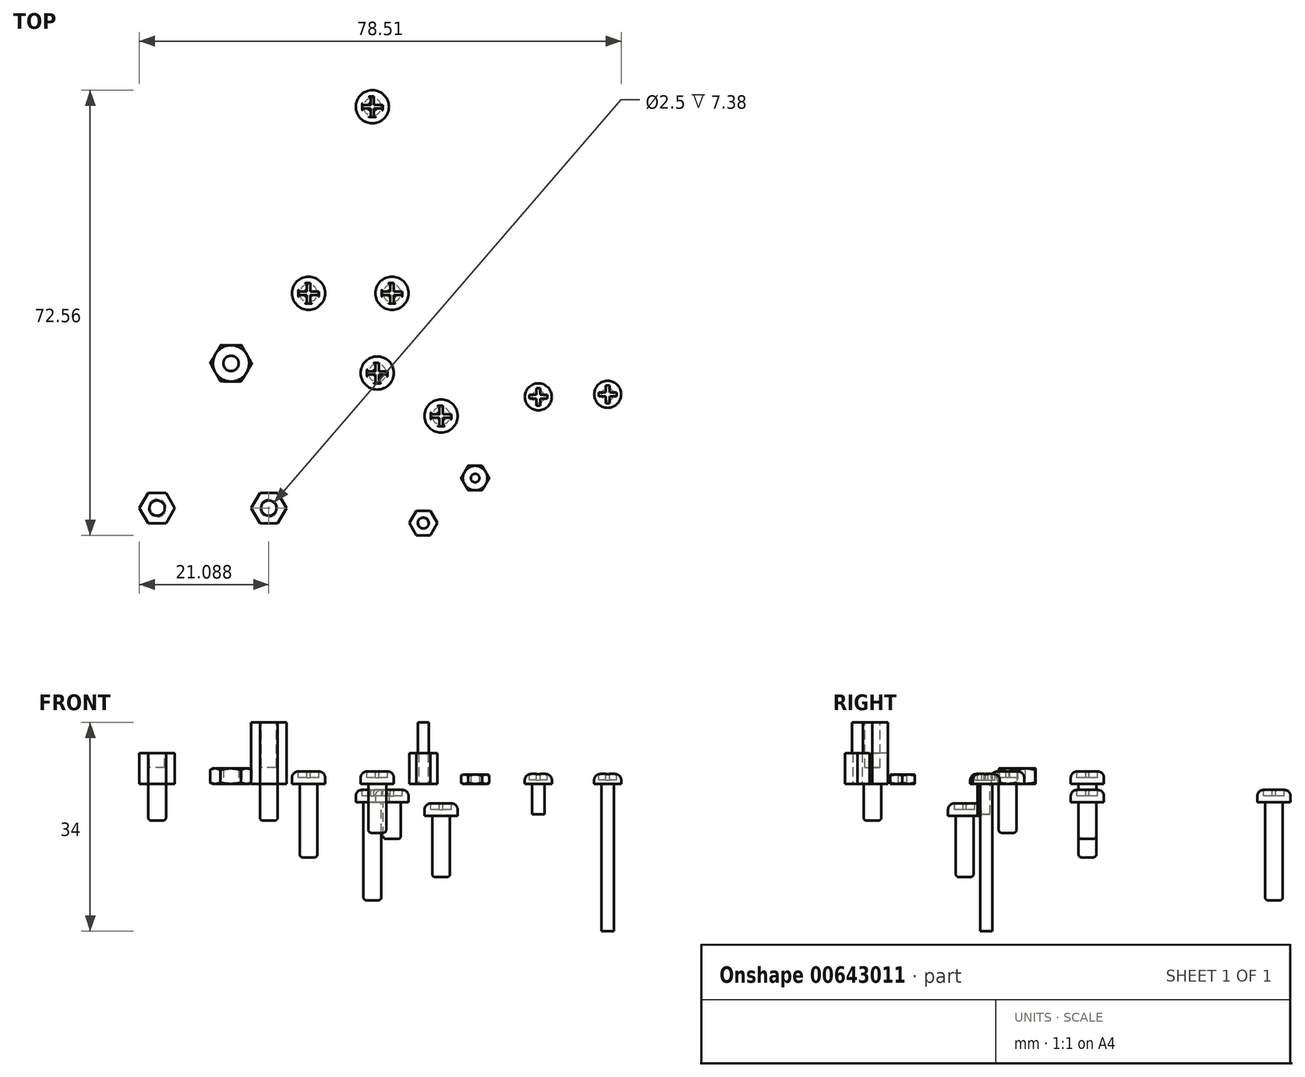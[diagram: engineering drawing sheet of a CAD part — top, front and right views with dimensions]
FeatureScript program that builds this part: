
annotation { "Feature Type Name" : "Feature", "Feature Type Description" : "" }
export const myFeature = defineFeature(function(context is Context, id is Id, definition is map)
    precondition{}
    {
        {
            var Q0;
            Q0=qCreatedBy(makeId("Top.planeOp"),FACE);
            var sketch = newSketch(context, id + "F0", { "sketchPlane" : qUnion([Q0])});
            skCircle(sketch, "E0.cCircle", {"center": v(-52.55, 30.34) * mm, "radius": 2.95 * mm, "construction": true});
            skLineSegment(sketch, "E0.0", {"start": v(-49.14, 30.28) * mm, "end": v(-50.9, 27.36) * mm});
            skLineSegment(sketch, "E0.1", {"start": v(-50.9, 27.36) * mm, "end": v(-54.3, 27.43) * mm});
            skLineSegment(sketch, "E0.2", {"start": v(-54.3, 27.43) * mm, "end": v(-55.95, 30.4) * mm});
            skLineSegment(sketch, "E0.3", {"start": v(-55.95, 30.4) * mm, "end": v(-54.2, 33.32) * mm});
            skLineSegment(sketch, "E0.4", {"start": v(-54.2, 33.32) * mm, "end": v(-50.79, 33.26) * mm});
            skLineSegment(sketch, "E0.5", {"start": v(-50.79, 33.26) * mm, "end": v(-49.14, 30.28) * mm});
            skPoint(sketch, "E0.0.midPoint", {"position": v(-50.02, 28.82) * mm});
            skCircle(sketch, "E1", {"center": v(-52.55, 30.34) * mm, "radius": 1.25 * mm});
            skSolve(sketch);
        }
        {
            var Q0;
            Q0=makeQuery(id+"F0.imprint","IMPRINT",FACE,{"disambiguationData":[TD([[makeQuery(id+"F0.imprint","IMPRINT",EDGE,{"derivedFrom":sQuery(id+"F0.wireOp",EDGE,"E0.0")}),-1.0]])]});
            extrude(context, id + "F1", {"entities" : qUnion([Q0]), "depth" : 2.5 * mm, "offsetDistance" : 25 * mm});
        }
        {
            var Q0;
            Q0=qCreatedBy(makeId("Top.planeOp"),FACE);
            var sketch = newSketch(context, id + "F2", { "sketchPlane" : qUnion([Q0])});
            skCircle(sketch, "E2", {"center": v(-39.92, 41.77) * mm, "radius": 2.7 * mm});
            skSolve(sketch);
        }
        {
            var Q0;
            Q0=makeQuery(id+"F2.imprint","IMPRINT",FACE,{"disambiguationData":[TD([[makeQuery(id+"F2.imprint","IMPRINT",EDGE,{"derivedFrom":sQuery(id+"F2.wireOp",EDGE,"E2")}),1.0]])]});
            extrude(context, id + "F3", {"entities" : qUnion([Q0]), "depth" : 2 * mm, "offsetDistance" : 25 * mm});
        }
        {
            var Q0;
            Q0=makeQuery(id+"F3.opExtrude","CAP_EDGE",EDGE,{"disambiguationData":[OSD([sQuery(id+"F2.wireOp",EDGE,"E2")])],"isStart":false});
            fillet(context, id + "F4", {"entities" : qUnion([Q0]), "radius" : 1 * mm, "tangentPropagation" : true, "allowEdgeOverflow" : false});
        }
        {
            var Q0;
            Q0=makeQuery(id+"F3.opExtrude","CAP_FACE",FACE,{"disambiguationData":[OSD([sQuery(id+"F2.wireOp",EDGE,"E2")])],"isStart":false});
            var sketch = newSketch(context, id + "F5", { "sketchPlane" : qUnion([Q0])});
            skLineSegment(sketch, "E3.bottom", {"start": v(-40.19, 43.45) * mm, "end": v(-39.65, 43.45) * mm});
            skLineSegment(sketch, "E3.top", {"start": v(-40.19, 40.1) * mm, "end": v(-39.65, 40.1) * mm});
            skLineSegment(sketch, "E3.left", {"start": v(-40.19, 43.45) * mm, "end": v(-40.19, 42.04) * mm});
            skLineSegment(sketch, "E3.right", {"start": v(-39.65, 43.45) * mm, "end": v(-39.65, 42.04) * mm});
            skPoint(sketch, "E3.middle", {"position": v(-39.92, 41.77) * mm});
            skLineSegment(sketch, "E4.bottom", {"start": v(-38.24, 42.04) * mm, "end": v(-38.24, 41.5) * mm});
            skLineSegment(sketch, "E4.top", {"start": v(-41.6, 42.04) * mm, "end": v(-41.6, 41.5) * mm});
            skLineSegment(sketch, "E4.left", {"start": v(-38.24, 42.04) * mm, "end": v(-39.65, 42.04) * mm});
            skLineSegment(sketch, "E4.right", {"start": v(-38.24, 41.5) * mm, "end": v(-39.65, 41.5) * mm});
            skLineSegment(sketch, "E5.trimOffspring", {"start": v(-40.19, 42.04) * mm, "end": v(-41.6, 42.04) * mm});
            skLineSegment(sketch, "E6.trimOffspring", {"start": v(-40.19, 41.5) * mm, "end": v(-40.19, 40.1) * mm});
            skLineSegment(sketch, "E7.trimOffspring", {"start": v(-40.19, 41.5) * mm, "end": v(-41.6, 41.5) * mm});
            skLineSegment(sketch, "E8.trimOffspring", {"start": v(-39.65, 41.5) * mm, "end": v(-39.65, 40.1) * mm});
            skSolve(sketch);
        }
        {
            var Q0;
            Q0=makeQuery(id+"F5.imprint","IMPRINT",FACE,{"disambiguationData":[TD([[makeQuery(id+"F5.imprint","IMPRINT",EDGE,{"derivedFrom":sQuery(id+"F5.wireOp",EDGE,"E3.bottom")}),-1.0]])]});
            extrude(context, id + "F6", {"entities" : qUnion([Q0]), "operationType" : NewBodyOperationType.REMOVE, "oppositeDirection" : true, "depth" : 1 * mm, "offsetDistance" : 25 * mm});
        }
        {
            var Q0;
            Q0=makeQuery(id+"F6.boolean.opBoolean","COPY",EDGE,{"derivedFrom":makeQuery(id+"F6.opExtrude","CAP_EDGE",EDGE,{"disambiguationData":[OSD([sQuery(id+"F5.wireOp",EDGE,"E4.left")])],"isStart":true})});
            var Q1;
            Q1=makeQuery(id+"F6.boolean.opBoolean","COPY",EDGE,{"derivedFrom":makeQuery(id+"F6.opExtrude","CAP_EDGE",EDGE,{"disambiguationData":[OSD([sQuery(id+"F5.wireOp",EDGE,"E3.right")])],"isStart":true})});
            var Q2;
            Q2=makeQuery(id+"F6.boolean.opBoolean","COPY",EDGE,{"derivedFrom":makeQuery(id+"F6.opExtrude","CAP_EDGE",EDGE,{"disambiguationData":[OSD([sQuery(id+"F5.wireOp",EDGE,"E3.left")])],"isStart":true})});
            var Q3;
            Q3=makeQuery(id+"F6.boolean.opBoolean","COPY",EDGE,{"derivedFrom":makeQuery(id+"F6.opExtrude","CAP_EDGE",EDGE,{"disambiguationData":[OSD([sQuery(id+"F5.wireOp",EDGE,"E5.trimOffspring")])],"isStart":true})});
            var Q4;
            Q4=makeQuery(id+"F6.boolean.opBoolean","COPY",EDGE,{"derivedFrom":makeQuery(id+"F6.opExtrude","CAP_EDGE",EDGE,{"disambiguationData":[OSD([sQuery(id+"F5.wireOp",EDGE,"E7.trimOffspring")])],"isStart":true})});
            var Q5;
            Q5=makeQuery(id+"F6.boolean.opBoolean","COPY",EDGE,{"derivedFrom":makeQuery(id+"F6.opExtrude","CAP_EDGE",EDGE,{"disambiguationData":[OSD([sQuery(id+"F5.wireOp",EDGE,"E6.trimOffspring")])],"isStart":true})});
            var Q6;
            Q6=makeQuery(id+"F6.boolean.opBoolean","COPY",EDGE,{"derivedFrom":makeQuery(id+"F6.opExtrude","CAP_EDGE",EDGE,{"disambiguationData":[OSD([sQuery(id+"F5.wireOp",EDGE,"E8.trimOffspring")])],"isStart":true})});
            var Q7;
            Q7=makeQuery(id+"F6.boolean.opBoolean","COPY",EDGE,{"derivedFrom":makeQuery(id+"F6.opExtrude","CAP_EDGE",EDGE,{"disambiguationData":[OSD([sQuery(id+"F5.wireOp",EDGE,"E4.right")])],"isStart":true})});
            fillet(context, id + "F7", {"entities" : qUnion([Q0, Q1, Q2, Q3, Q4, Q5, Q6, Q7]), "radius" : 0.3 * mm, "tangentPropagation" : true, "allowEdgeOverflow" : false});
        }
        {
            var Q0;
            Q0=makeQuery(id+"F3.opExtrude","CAP_FACE",FACE,{"disambiguationData":[OSD([sQuery(id+"F2.wireOp",EDGE,"E2")])],"isStart":true});
            var sketch = newSketch(context, id + "F8", { "sketchPlane" : qUnion([Q0])});
            skCircle(sketch, "E9.0", {"center": v(-39.92, -41.77) * mm, "radius": 2.7 * mm});
            skCircle(sketch, "E10", {"center": v(-39.92, -41.77) * mm, "radius": 1.45 * mm});
            skSolve(sketch);
        }
        {
            var Q0;
            Q0=makeQuery(id+"F3.opExtrude","SWEPT_BODY",BODY,{"disambiguationData":[OSD([sQuery(id+"F2.wireOp",EDGE,"E2")])]});
            transform(context, id + "F9", {"entities" : qUnion([Q0]), "transformType" : TransformType.TRANSLATION_3D, "dx" : 13.6 * mm, "dy" : 0 * mm, "dz" : -3 * mm, "makeCopy" : true});
        }
        {
            var Q0;
            Q0=makeQuery(id+"F9.opPattern","COPY",BODY,{"derivedFrom":makeQuery(id+"F3.opExtrude","SWEPT_BODY",BODY,{"disambiguationData":[OSD([sQuery(id+"F2.wireOp",EDGE,"E2")])]}),"instanceName":"1"});
            transform(context, id + "F10", {"entities" : qUnion([Q0]), "transformType" : TransformType.TRANSLATION_3D, "dx" : -3.2 * mm, "dy" : 30.4 * mm, "dz" : 0 * mm, "makeCopy" : true});
        }
        {
            var Q0;
            Q0=makeQuery(id+"F3.opExtrude","SWEPT_BODY",BODY,{"disambiguationData":[OSD([sQuery(id+"F2.wireOp",EDGE,"E2")])]});
            transform(context, id + "F11", {"entities" : qUnion([Q0]), "transformType" : TransformType.TRANSLATION_3D, "dx" : 16.3 * mm, "dy" : -46.7 * mm, "dz" : 0 * mm, "makeCopy" : true});
        }
        {
            var Q0;
            Q0=makeQuery(id+"F3.opExtrude","SWEPT_BODY",BODY,{"disambiguationData":[OSD([sQuery(id+"F2.wireOp",EDGE,"E2")])]});
            transform(context, id + "F12", {"entities" : qUnion([Q0]), "transformType" : TransformType.TRANSLATION_3D, "dx" : 11.2 * mm, "dy" : -13 * mm, "dz" : 0 * mm, "makeCopy" : true});
        }
        {
            var Q0;
            Q0=makeQuery(id+"F8.imprint","IMPRINT",FACE,{"disambiguationData":[TD([[makeQuery(id+"F8.imprint","IMPRINT",EDGE,{"derivedFrom":sQuery(id+"F8.wireOp",EDGE,"E10")}),1.0]])]});
            extrude(context, id + "F13", {"entities" : qUnion([Q0]), "operationType" : NewBodyOperationType.ADD, "depth" : 12 * mm, "offsetDistance" : 25 * mm});
        }
        {
            var Q0;
            Q0=makeQuery(id+"F13.opExtrude","CAP_EDGE",EDGE,{"disambiguationData":[OSD([sQuery(id+"F8.wireOp",EDGE,"E10")])],"isStart":false});
            fillet(context, id + "F14", {"entities" : qUnion([Q0]), "radius" : 0.5 * mm, "tangentPropagation" : true, "allowEdgeOverflow" : false});
        }
        {
            var Q0;
            Q0=makeQuery(id+"F9.opPattern","COPY",FACE,{"derivedFrom":makeQuery(id+"F3.opExtrude","CAP_FACE",FACE,{"disambiguationData":[OSD([sQuery(id+"F2.wireOp",EDGE,"E2")])],"isStart":true}),"instanceName":"1"});
            var sketch = newSketch(context, id + "F15", { "sketchPlane" : qUnion([Q0])});
            skCircle(sketch, "E11.0", {"center": v(-26.32, -41.77) * mm, "radius": 2.7 * mm});
            skCircle(sketch, "E12", {"center": v(-26.32, -41.77) * mm, "radius": 1.45 * mm});
            skSolve(sketch);
        }
        {
            var Q0;
            Q0=makeQuery(id+"F15.imprint","IMPRINT",FACE,{"disambiguationData":[TD([[makeQuery(id+"F15.imprint","IMPRINT",EDGE,{"derivedFrom":sQuery(id+"F15.wireOp",EDGE,"E12")}),1.0]])]});
            extrude(context, id + "F16", {"entities" : qUnion([Q0]), "operationType" : NewBodyOperationType.ADD, "depth" : 6 * mm, "offsetDistance" : 25 * mm});
        }
        {
            var Q0;
            Q0=makeQuery(id+"F16.opExtrude","CAP_EDGE",EDGE,{"disambiguationData":[OSD([sQuery(id+"F15.wireOp",EDGE,"E12")])],"isStart":false});
            fillet(context, id + "F17", {"entities" : qUnion([Q0]), "radius" : 0.5 * mm, "tangentPropagation" : true, "allowEdgeOverflow" : false});
        }
        {
            var Q0;
            Q0=makeQuery(id+"F11.opPattern","COPY",BODY,{"derivedFrom":makeQuery(id+"F3.opExtrude","SWEPT_BODY",BODY,{"disambiguationData":[OSD([sQuery(id+"F2.wireOp",EDGE,"E2")])]}),"instanceName":"1"});
            transform(context, id + "F18", {"entities" : qUnion([Q0]), "transformType" : TransformType.TRANSLATION_3D, "dx" : 7.2 * mm, "dy" : 0 * mm, "dz" : 30.6 * mm, "makeCopy" : false});
        }
        {
            var Q0;
            Q0=makeQuery(id+"F11.opPattern","COPY",BODY,{"derivedFrom":makeQuery(id+"F3.opExtrude","SWEPT_BODY",BODY,{"disambiguationData":[OSD([sQuery(id+"F2.wireOp",EDGE,"E2")])]}),"instanceName":"1"});
            transform(context, id + "F19", {"entities" : qUnion([Q0]), "transformType" : TransformType.TRANSLATION_3D, "dx" : -1.9 * mm, "dy" : 26.7 * mm, "dz" : -35.8 * mm, "makeCopy" : false});
        }
        {
            var Q0;
            Q0=makeQuery(id+"F11.opPattern","COPY",FACE,{"derivedFrom":makeQuery(id+"F3.opExtrude","CAP_FACE",FACE,{"disambiguationData":[OSD([sQuery(id+"F2.wireOp",EDGE,"E2")])],"isStart":true}),"instanceName":"1"});
            var sketch = newSketch(context, id + "F20", { "sketchPlane" : qUnion([Q0])});
            skCircle(sketch, "E13.0", {"center": v(-18.32, -21.77) * mm, "radius": 2.7 * mm});
            skCircle(sketch, "E14", {"center": v(-18.32, -21.77) * mm, "radius": 1.45 * mm});
            skSolve(sketch);
        }
        {
            var Q0;
            Q0=makeQuery(id+"F20.imprint","IMPRINT",FACE,{"disambiguationData":[TD([[makeQuery(id+"F20.imprint","IMPRINT",EDGE,{"derivedFrom":sQuery(id+"F20.wireOp",EDGE,"E14")}),1.0]])]});
            extrude(context, id + "F21", {"entities" : qUnion([Q0]), "operationType" : NewBodyOperationType.ADD, "depth" : 10 * mm, "offsetDistance" : 25 * mm});
        }
        {
            var Q0;
            Q0=makeQuery(id+"F21.opExtrude","CAP_EDGE",EDGE,{"disambiguationData":[OSD([sQuery(id+"F20.wireOp",EDGE,"E14")])],"isStart":false});
            fillet(context, id + "F22", {"entities" : qUnion([Q0]), "radius" : 0.5 * mm, "tangentPropagation" : true, "allowEdgeOverflow" : false});
        }
        {
            var Q0;
            Q0=makeQuery(id+"F12.opPattern","COPY",FACE,{"derivedFrom":makeQuery(id+"F3.opExtrude","CAP_FACE",FACE,{"disambiguationData":[OSD([sQuery(id+"F2.wireOp",EDGE,"E2")])],"isStart":true}),"instanceName":"1"});
            var sketch = newSketch(context, id + "F23", { "sketchPlane" : qUnion([Q0])});
            skCircle(sketch, "E15.0", {"center": v(-28.72, -28.77) * mm, "radius": 2.7 * mm});
            skCircle(sketch, "E16", {"center": v(-28.72, -28.77) * mm, "radius": 1.45 * mm});
            skSolve(sketch);
        }
        {
            var Q0;
            Q0=makeQuery(id+"F23.imprint","IMPRINT",FACE,{"disambiguationData":[TD([[makeQuery(id+"F23.imprint","IMPRINT",EDGE,{"derivedFrom":sQuery(id+"F23.wireOp",EDGE,"E16")}),1.0]])]});
            extrude(context, id + "F24", {"entities" : qUnion([Q0]), "operationType" : NewBodyOperationType.ADD, "depth" : 8 * mm, "offsetDistance" : 25 * mm});
        }
        {
            var Q0;
            Q0=makeQuery(id+"F24.opExtrude","CAP_EDGE",EDGE,{"disambiguationData":[OSD([sQuery(id+"F23.wireOp",EDGE,"E16")])],"isStart":false});
            fillet(context, id + "F25", {"entities" : qUnion([Q0]), "radius" : 0.5 * mm, "tangentPropagation" : true, "allowEdgeOverflow" : false});
        }
        {
            var Q0;
            Q0=qCreatedBy(makeId("Top.planeOp"),FACE);
            var sketch = newSketch(context, id + "F26", { "sketchPlane" : qUnion([Q0])});
            skCircle(sketch, "E17.cCircle", {"center": v(-46.4, 6.75) * mm, "radius": 2.5 * mm, "construction": true});
            skLineSegment(sketch, "E17.0", {"start": v(-43.5, 6.75) * mm, "end": v(-44.95, 4.25) * mm});
            skLineSegment(sketch, "E17.1", {"start": v(-44.95, 4.25) * mm, "end": v(-47.84, 4.25) * mm});
            skLineSegment(sketch, "E17.2", {"start": v(-47.84, 4.25) * mm, "end": v(-49.28, 6.75) * mm});
            skLineSegment(sketch, "E17.3", {"start": v(-49.28, 6.75) * mm, "end": v(-47.84, 9.25) * mm});
            skLineSegment(sketch, "E17.4", {"start": v(-47.84, 9.25) * mm, "end": v(-44.95, 9.25) * mm});
            skLineSegment(sketch, "E17.5", {"start": v(-44.95, 9.25) * mm, "end": v(-43.5, 6.75) * mm});
            skPoint(sketch, "E17.0.midPoint", {"position": v(-44.23, 5.5) * mm});
            skSolve(sketch);
        }
        {
            var Q0;
            Q0=makeQuery(id+"F26.imprint","IMPRINT",FACE,{"disambiguationData":[TD([[makeQuery(id+"F26.imprint","IMPRINT",EDGE,{"derivedFrom":sQuery(id+"F26.wireOp",EDGE,"E17.0")}),-1.0]])]});
            extrude(context, id + "F27", {"entities" : qUnion([Q0]), "depth" : 10 * mm, "offsetDistance" : 25 * mm});
        }
        {
            var Q0;
            Q0=makeQuery(id+"F27.opExtrude","CAP_FACE",FACE,{"disambiguationData":[OSD([sQuery(id+"F26.wireOp",EDGE,"E17.0"),sQuery(id+"F26.wireOp",EDGE,"E17.1"),sQuery(id+"F26.wireOp",EDGE,"E17.2"),sQuery(id+"F26.wireOp",EDGE,"E17.3"),sQuery(id+"F26.wireOp",EDGE,"E17.4"),sQuery(id+"F26.wireOp",EDGE,"E17.5")])],"isStart":false});
            var sketch = newSketch(context, id + "F28", { "sketchPlane" : qUnion([Q0])});
            skCircle(sketch, "E18", {"center": v(-46.4, 6.75) * mm, "radius": 1.25 * mm});
            skPoint(sketch, "E18.centerSnap0", {"position": v(-46.4, 9.25) * mm});
            skSolve(sketch);
        }
        {
            var Q0;
            Q0=makeQuery(id+"F28.imprint","IMPRINT",FACE,{"disambiguationData":[TD([[makeQuery(id+"F28.imprint","IMPRINT",EDGE,{"derivedFrom":sQuery(id+"F28.wireOp",EDGE,"E18")}),1.0]])]});
            extrude(context, id + "F29", {"entities" : qUnion([Q0]), "operationType" : NewBodyOperationType.REMOVE, "oppositeDirection" : true, "depth" : 7.38 * mm, "offsetDistance" : 25 * mm});
        }
        {
            var Q0;
            Q0=makeQuery(id+"F27.opExtrude","CAP_FACE",FACE,{"disambiguationData":[OSD([sQuery(id+"F26.wireOp",EDGE,"E17.0"),sQuery(id+"F26.wireOp",EDGE,"E17.1"),sQuery(id+"F26.wireOp",EDGE,"E17.2"),sQuery(id+"F26.wireOp",EDGE,"E17.3"),sQuery(id+"F26.wireOp",EDGE,"E17.4"),sQuery(id+"F26.wireOp",EDGE,"E17.5")])],"isStart":true});
            var sketch = newSketch(context, id + "F30", { "sketchPlane" : qUnion([Q0])});
            skCircle(sketch, "E19", {"center": v(-46.4, -6.75) * mm, "radius": 1.45 * mm});
            skPoint(sketch, "E19.centerSnap0", {"position": v(-46.4, -9.25) * mm});
            skSolve(sketch);
        }
        {
            var Q0;
            Q0=makeQuery(id+"F30.imprint","IMPRINT",FACE,{"disambiguationData":[TD([[makeQuery(id+"F30.imprint","IMPRINT",EDGE,{"derivedFrom":sQuery(id+"F30.wireOp",EDGE,"E19")}),1.0]])]});
            extrude(context, id + "F31", {"entities" : qUnion([Q0]), "operationType" : NewBodyOperationType.ADD, "depth" : 6 * mm, "offsetDistance" : 25 * mm});
        }
        {
            var Q0;
            Q0=makeQuery(id+"F31.opExtrude","CAP_EDGE",EDGE,{"disambiguationData":[OSD([sQuery(id+"F30.wireOp",EDGE,"E19")])],"isStart":false});
            fillet(context, id + "F32", {"entities" : qUnion([Q0]), "radius" : 0.5 * mm, "tangentPropagation" : true, "allowEdgeOverflow" : false});
        }
        {
            var Q0;
            Q0=makeQuery(id+"F1.opExtrude","CAP_EDGE",EDGE,{"disambiguationData":[OSD([sQuery(id+"F0.wireOp",EDGE,"E0.0")])],"isStart":false});
            cPoint(context, id + "F33", {"entities" : qUnion([Q0]), "parameter" : 0.5});
        }
        {
            var Q0;
            Q0=makeQuery(id+"F1.opExtrude","CAP_EDGE",EDGE,{"disambiguationData":[OSD([sQuery(id+"F0.wireOp",EDGE,"E0.3")])],"isStart":false});
            cPoint(context, id + "F34", {"entities" : qUnion([Q0]), "parameter" : 0.5});
        }
        {
            var Q0;
            Q0=makeQuery(id+"F1.opExtrude","CAP_EDGE",EDGE,{"disambiguationData":[OSD([sQuery(id+"F0.wireOp",EDGE,"E0.0")])],"isStart":true});
            cPoint(context, id + "F35", {"entities" : qUnion([Q0]), "parameter" : 0.5});
        }
        {
            var Q0;
            Q0 = qCreatedBy(id + "F33" ,VERTEX);
            var Q1;
            Q1 = qCreatedBy(id + "F34" ,VERTEX);
            var Q2;
            Q2 = qCreatedBy(id + "F35" ,VERTEX);
            cPlane(context, id + "F36", {"entities" : qUnion([Q0, Q1, Q2]), "cplaneType" : CPlaneType.THREE_POINT, "offset" : 25 * mm, "width" : 150 * mm, "height" : 150 * mm});
        }
        {
            var Q0;
            Q0=qCreatedBy(id+"F36.planeOp",FACE);
            var sketch = newSketch(context, id + "F37", { "sketchPlane" : qUnion([Q0])});
            skLineSegment(sketch, "E20", {"start": v(63.62, 2.5) * mm, "end": v(66, 1.13) * mm});
            skLineSegment(sketch, "E21", {"start": v(63.62, 0) * mm, "end": v(66, 1.12) * mm});
            skLineSegment(sketch, "E22", {"start": v(63.62, 2.5) * mm, "end": v(66, 2.5) * mm});
            skLineSegment(sketch, "E23", {"start": v(66, 2.5) * mm, "end": v(66, 1.13) * mm});
            skLineSegment(sketch, "E24", {"start": v(66, 1.13) * mm, "end": v(66, 0) * mm});
            skLineSegment(sketch, "E25", {"start": v(66, 0) * mm, "end": v(63.62, 0) * mm});
            skSolve(sketch);
        }
        {
            var Q0;
            Q0=makeQuery(id+"F37.imprint","IMPRINT",FACE,{"disambiguationData":[TD([[makeQuery(id+"F37.imprint","IMPRINT",EDGE,{"derivedFrom":sQuery(id+"F37.wireOp",EDGE,"E20")}),1.0]])]});
            var Q1;
            Q1=makeQuery(id+"F37.imprint","IMPRINT",FACE,{"disambiguationData":[TD([[makeQuery(id+"F37.imprint","IMPRINT",EDGE,{"derivedFrom":sQuery(id+"F37.wireOp",EDGE,"E21")}),-1.0]])]});
            var Q2;
            Q2=makeQuery(id+"F1.opExtrude","CAP_EDGE",EDGE,{"disambiguationData":[OSD([sQuery(id+"F0.wireOp",EDGE,"E1")])],"isStart":false});
            revolve(context, id + "F38", {"operationType" : NewBodyOperationType.REMOVE, "entities" : qUnion([Q0, Q1]), "axis" : qUnion([Q2]), "revolveType" : RevolveType.FULL, "oppositeDirection" : true});
        }
        {
            var Q0;
            Q0=qCreatedBy(makeId("Top.planeOp"),FACE);
            var sketch = newSketch(context, id + "F39", { "sketchPlane" : qUnion([Q0])});
            skCircle(sketch, "E26.cCircle", {"center": v(-21.21, 4.3) * mm, "radius": 2 * mm, "construction": true});
            skLineSegment(sketch, "E26.0", {"start": v(-18.9, 4.3) * mm, "end": v(-20.06, 2.3) * mm});
            skLineSegment(sketch, "E26.1", {"start": v(-20.06, 2.3) * mm, "end": v(-22.37, 2.3) * mm});
            skLineSegment(sketch, "E26.2", {"start": v(-22.37, 2.3) * mm, "end": v(-23.52, 4.3) * mm});
            skLineSegment(sketch, "E26.3", {"start": v(-23.52, 4.3) * mm, "end": v(-22.37, 6.3) * mm});
            skLineSegment(sketch, "E26.4", {"start": v(-22.37, 6.3) * mm, "end": v(-20.06, 6.3) * mm});
            skLineSegment(sketch, "E26.5", {"start": v(-20.06, 6.3) * mm, "end": v(-18.9, 4.3) * mm});
            skPoint(sketch, "E26.0.midPoint", {"position": v(-19.48, 3.3) * mm});
            skCircle(sketch, "E27", {"center": v(-21.21, 4.3) * mm, "radius": 0.75 * mm});
            skSolve(sketch);
        }
        {
            var Q0;
            Q0=makeQuery(id+"F39.imprint","IMPRINT",FACE,{"disambiguationData":[TD([[makeQuery(id+"F39.imprint","IMPRINT",EDGE,{"derivedFrom":sQuery(id+"F39.wireOp",EDGE,"E26.0")}),-1.0]])]});
            extrude(context, id + "F40", {"entities" : qUnion([Q0]), "depth" : 5 * mm, "offsetDistance" : 25 * mm});
        }
        {
            var Q0;
            Q0=makeQuery(id+"F40.opExtrude","CAP_FACE",FACE,{"disambiguationData":[OSD([sQuery(id+"F39.wireOp",EDGE,"E26.0"),sQuery(id+"F39.wireOp",EDGE,"E26.1"),sQuery(id+"F39.wireOp",EDGE,"E26.2"),sQuery(id+"F39.wireOp",EDGE,"E26.3"),sQuery(id+"F39.wireOp",EDGE,"E26.4"),sQuery(id+"F39.wireOp",EDGE,"E26.5"),sQuery(id+"F39.wireOp",EDGE,"E27")])],"isStart":false});
            var sketch = newSketch(context, id + "F41", { "sketchPlane" : qUnion([Q0])});
            skCircle(sketch, "E28", {"center": v(-21.21, 4.3) * mm, "radius": 0.9 * mm});
            skSolve(sketch);
        }
        {
            var Q0;
            Q0=makeQuery(id+"F41.imprint","IMPRINT",FACE,{"disambiguationData":[TD([[makeQuery(id+"F41.imprint","IMPRINT",EDGE,{"derivedFrom":makeQuery(id+"F40.opExtrude","CAP_EDGE",EDGE,{"disambiguationData":[OSD([sQuery(id+"F39.wireOp",EDGE,"E27")])],"isStart":false})}),1.0]])]});
            var Q1;
            Q1=makeQuery(id+"F41.imprint","IMPRINT",FACE,{"disambiguationData":[TD([[makeQuery(id+"F41.imprint","IMPRINT",EDGE,{"derivedFrom":sQuery(id+"F41.wireOp",EDGE,"E28")}),1.0]])]});
            extrude(context, id + "F42", {"entities" : qUnion([Q0, Q1]), "operationType" : NewBodyOperationType.ADD, "depth" : 5 * mm, "offsetDistance" : 25 * mm});
        }
        {
            var Q0;
            Q0=qCreatedBy(makeId("Top.planeOp"),FACE);
            var sketch = newSketch(context, id + "F43", { "sketchPlane" : qUnion([Q0])});
            skCircle(sketch, "E29.cCircle", {"center": v(-12.77, 11.64) * mm, "radius": 2 * mm, "construction": true});
            skLineSegment(sketch, "E29.0", {"start": v(-10.46, 11.64) * mm, "end": v(-11.61, 9.64) * mm});
            skLineSegment(sketch, "E29.1", {"start": v(-11.61, 9.64) * mm, "end": v(-13.92, 9.64) * mm});
            skLineSegment(sketch, "E29.2", {"start": v(-13.92, 9.64) * mm, "end": v(-15.08, 11.64) * mm});
            skLineSegment(sketch, "E29.3", {"start": v(-15.08, 11.64) * mm, "end": v(-13.92, 13.64) * mm});
            skLineSegment(sketch, "E29.4", {"start": v(-13.92, 13.64) * mm, "end": v(-11.61, 13.64) * mm});
            skLineSegment(sketch, "E29.5", {"start": v(-11.61, 13.64) * mm, "end": v(-10.46, 11.64) * mm});
            skPoint(sketch, "E29.0.midPoint", {"position": v(-11.03, 10.64) * mm});
            skCircle(sketch, "E30", {"center": v(-12.77, 11.64) * mm, "radius": 0.7 * mm});
            skSolve(sketch);
        }
        {
            var Q0;
            Q0 = qSketchRegion(id + "F43", true);
            extrude(context, id + "F44", {"entities" : qUnion([Q0]), "depth" : 1.5 * mm, "offsetDistance" : 25 * mm});
        }
        {
            var Q0;
            Q0=qCreatedBy(makeId("Top.planeOp"),FACE);
            var sketch = newSketch(context, id + "F45", { "sketchPlane" : qUnion([Q0])});
            skCircle(sketch, "E31", {"center": v(-2.47, 24.89) * mm, "radius": 2.2 * mm});
            skSolve(sketch);
        }
        {
            var Q0;
            Q0 = qSketchRegion(id + "F45", true);
            extrude(context, id + "F46", {"entities" : qUnion([Q0]), "depth" : 1.6 * mm, "offsetDistance" : 25 * mm});
        }
        {
            var Q0;
            Q0=makeQuery(id+"F46.opExtrude","CAP_FACE",FACE,{"disambiguationData":[OSD([sQuery(id+"F45.wireOp",EDGE,"E31")])],"isStart":false});
            var sketch = newSketch(context, id + "F47", { "sketchPlane" : qUnion([Q0])});
            skCircle(sketch, "E32.0", {"center": v(-2.47, 24.89) * mm, "radius": 2.2 * mm});
            skLineSegment(sketch, "E33.bottom", {"start": v(-1.03, 24.58) * mm, "end": v(-2.16, 24.58) * mm});
            skLineSegment(sketch, "E33.top", {"start": v(-1.03, 25.2) * mm, "end": v(-2.16, 25.2) * mm});
            skLineSegment(sketch, "E33.left", {"start": v(-1.03, 24.58) * mm, "end": v(-1.03, 25.2) * mm});
            skLineSegment(sketch, "E33.right", {"start": v(-3.91, 24.58) * mm, "end": v(-3.91, 25.2) * mm});
            skLineSegment(sketch, "E34.bottom", {"start": v(-2.79, 23.45) * mm, "end": v(-2.79, 24.58) * mm});
            skLineSegment(sketch, "E34.top", {"start": v(-2.16, 23.45) * mm, "end": v(-2.16, 24.58) * mm});
            skLineSegment(sketch, "E34.left", {"start": v(-2.79, 23.45) * mm, "end": v(-2.16, 23.45) * mm});
            skLineSegment(sketch, "E34.right", {"start": v(-2.79, 26.33) * mm, "end": v(-2.16, 26.33) * mm});
            skLineSegment(sketch, "E35.trimOffspring", {"start": v(-2.79, 25.2) * mm, "end": v(-3.91, 25.2) * mm});
            skLineSegment(sketch, "E36.trimOffspring", {"start": v(-2.79, 25.2) * mm, "end": v(-2.79, 26.33) * mm});
            skLineSegment(sketch, "E37.trimOffspring", {"start": v(-2.79, 24.58) * mm, "end": v(-3.91, 24.58) * mm});
            skLineSegment(sketch, "E38.trimOffspring", {"start": v(-2.16, 25.2) * mm, "end": v(-2.16, 26.33) * mm});
            skSolve(sketch);
        }
        {
            var Q0;
            Q0=makeQuery(id+"F47.imprint","IMPRINT",FACE,{"disambiguationData":[TD([[makeQuery(id+"F47.imprint","IMPRINT",EDGE,{"derivedFrom":sQuery(id+"F47.wireOp",EDGE,"E33.bottom")}),-1.0]])]});
            extrude(context, id + "F48", {"entities" : qUnion([Q0]), "operationType" : NewBodyOperationType.REMOVE, "oppositeDirection" : true, "depth" : 1 * mm, "offsetDistance" : 25 * mm});
        }
        {
            var Q0;
            Q0=makeQuery(id+"F46.opExtrude","CAP_EDGE",EDGE,{"disambiguationData":[OSD([sQuery(id+"F45.wireOp",EDGE,"E31")])],"isStart":false});
            fillet(context, id + "F49", {"entities" : qUnion([Q0]), "radius" : 1 * mm, "tangentPropagation" : true, "allowEdgeOverflow" : false});
        }
        {
            var Q0;
            Q0=makeQuery(id+"F46.opExtrude","SWEPT_BODY",BODY,{"disambiguationData":[OSD([sQuery(id+"F45.wireOp",EDGE,"E31")])]});
            transform(context, id + "F50", {"entities" : qUnion([Q0]), "transformType" : TransformType.TRANSLATION_3D, "dx" : 11.3 * mm, "dy" : 0.4 * mm, "dz" : 0 * mm, "makeCopy" : true});
        }
        {
            var Q0;
            Q0=makeQuery(id+"F46.opExtrude","CAP_FACE",FACE,{"disambiguationData":[OSD([sQuery(id+"F45.wireOp",EDGE,"E31")])],"isStart":true});
            var sketch = newSketch(context, id + "F51", { "sketchPlane" : qUnion([Q0])});
            skCircle(sketch, "E39.0", {"center": v(-2.47, -24.89) * mm, "radius": 2.2 * mm});
            skCircle(sketch, "E40", {"center": v(-2.47, -24.89) * mm, "radius": 1 * mm});
            skSolve(sketch);
        }
        {
            var Q0;
            Q0=makeQuery(id+"F51.imprint","IMPRINT",FACE,{"disambiguationData":[TD([[makeQuery(id+"F51.imprint","IMPRINT",EDGE,{"derivedFrom":sQuery(id+"F51.wireOp",EDGE,"E40")}),1.0]])]});
            extrude(context, id + "F52", {"entities" : qUnion([Q0]), "operationType" : NewBodyOperationType.ADD, "depth" : 5 * mm, "offsetDistance" : 25 * mm});
        }
        {
            var Q0;
            Q0=makeQuery(id+"F27.opExtrude","SWEPT_BODY",BODY,{"disambiguationData":[OSD([sQuery(id+"F26.wireOp",EDGE,"E17.0"),sQuery(id+"F26.wireOp",EDGE,"E17.1"),sQuery(id+"F26.wireOp",EDGE,"E17.2"),sQuery(id+"F26.wireOp",EDGE,"E17.3"),sQuery(id+"F26.wireOp",EDGE,"E17.4"),sQuery(id+"F26.wireOp",EDGE,"E17.5")])]});
            transform(context, id + "F53", {"entities" : qUnion([Q0]), "transformType" : TransformType.TRANSLATION_3D, "dx" : -18.2 * mm, "dy" : 0 * mm, "dz" : 0 * mm, "makeCopy" : true});
        }
        {
            var Q0;
            Q0=makeQuery(id+"F53.opPattern","COPY",FACE,{"derivedFrom":makeQuery(id+"F27.opExtrude","CAP_FACE",FACE,{"disambiguationData":[OSD([sQuery(id+"F26.wireOp",EDGE,"E17.0"),sQuery(id+"F26.wireOp",EDGE,"E17.1"),sQuery(id+"F26.wireOp",EDGE,"E17.2"),sQuery(id+"F26.wireOp",EDGE,"E17.3"),sQuery(id+"F26.wireOp",EDGE,"E17.4"),sQuery(id+"F26.wireOp",EDGE,"E17.5")])],"isStart":false}),"instanceName":"1"});
            var sketch = newSketch(context, id + "F54", { "sketchPlane" : qUnion([Q0])});
            skCircle(sketch, "E41", {"center": v(-64.6, 6.75) * mm, "radius": 7.5 * mm});
            skSolve(sketch);
        }
        {
            var Q0;
            Q0=makeQuery(id+"F54.imprint","IMPRINT",FACE,{"disambiguationData":[TD([[makeQuery(id+"F54.imprint","IMPRINT",EDGE,{"derivedFrom":sQuery(id+"F54.wireOp",EDGE,"E41")}),1.0]])]});
            var Q1;
            Q1=makeQuery(id+"F54.imprint","IMPRINT",FACE,{"disambiguationData":[TD([[makeQuery(id+"F54.imprint","IMPRINT",EDGE,{"derivedFrom":makeQuery(id+"F53.opPattern","COPY",EDGE,{"derivedFrom":makeQuery(id+"F27.opExtrude","CAP_EDGE",EDGE,{"disambiguationData":[OSD([sQuery(id+"F26.wireOp",EDGE,"E17.0")])],"isStart":false}),"instanceName":"1"})}),-1.0]])]});
            extrude(context, id + "F55", {"entities" : qUnion([Q0, Q1]), "operationType" : NewBodyOperationType.REMOVE, "oppositeDirection" : true, "depth" : 5 * mm, "offsetDistance" : 25 * mm});
        }
        {
            var Q0;
            Q0=makeQuery(id+"F50.opPattern","COPY",FACE,{"derivedFrom":makeQuery(id+"F46.opExtrude","CAP_FACE",FACE,{"disambiguationData":[OSD([sQuery(id+"F45.wireOp",EDGE,"E31")])],"isStart":true}),"instanceName":"1"});
            var sketch = newSketch(context, id + "F56", { "sketchPlane" : qUnion([Q0])});
            skCircle(sketch, "E42", {"center": v(8.83, -25.29) * mm, "radius": 1 * mm});
            skSolve(sketch);
        }
        {
            var Q0;
            Q0=makeQuery(id+"F56.imprint","IMPRINT",FACE,{"disambiguationData":[TD([[makeQuery(id+"F56.imprint","IMPRINT",EDGE,{"derivedFrom":sQuery(id+"F56.wireOp",EDGE,"E42")}),1.0]])]});
            extrude(context, id + "F57", {"entities" : qUnion([Q0]), "operationType" : NewBodyOperationType.ADD, "depth" : 24 * mm, "offsetDistance" : 25 * mm});
        }
        {
            var Q0;
            Q0=makeQuery(id+"F44.opExtrude","CAP_EDGE",EDGE,{"disambiguationData":[OSD([sQuery(id+"F43.wireOp",EDGE,"E29.5")])],"isStart":false});
            cPoint(context, id + "F58", {"entities" : qUnion([Q0]), "parameter" : 0.5});
        }
        {
            var Q0;
            Q0=makeQuery(id+"F44.opExtrude","CAP_EDGE",EDGE,{"disambiguationData":[OSD([sQuery(id+"F43.wireOp",EDGE,"E29.2")])],"isStart":false});
            cPoint(context, id + "F59", {"entities" : qUnion([Q0]), "parameter" : 0.5});
        }
        {
            var Q0;
            Q0=makeQuery(id+"F44.opExtrude","CAP_EDGE",EDGE,{"disambiguationData":[OSD([sQuery(id+"F43.wireOp",EDGE,"E29.5")])],"isStart":true});
            cPoint(context, id + "F60", {"entities" : qUnion([Q0]), "parameter" : 0.5});
        }
        {
            var Q0;
            Q0 = qCreatedBy(id + "F58" ,VERTEX);
            var Q1;
            Q1 = qCreatedBy(id + "F59" ,VERTEX);
            var Q2;
            Q2 = qCreatedBy(id + "F60" ,VERTEX);
            cPlane(context, id + "F61", {"entities" : qUnion([Q0, Q1, Q2]), "cplaneType" : CPlaneType.THREE_POINT, "offset" : 25 * mm, "width" : 150 * mm, "height" : 150 * mm});
        }
        {
            var Q0;
            Q0=qCreatedBy(id+"F61.planeOp",FACE);
            var sketch = newSketch(context, id + "F62", { "sketchPlane" : qUnion([Q0])});
            skLineSegment(sketch, "E43", {"start": v(3.24, 1.5) * mm, "end": v(1.94, 0.75) * mm});
            skLineSegment(sketch, "E44", {"start": v(1.94, 0.75) * mm, "end": v(3.24, 0) * mm});
            skLineSegment(sketch, "E45", {"start": v(3.24, 1.5) * mm, "end": v(1.94, 1.5) * mm});
            skLineSegment(sketch, "E46", {"start": v(1.94, 1.5) * mm, "end": v(1.94, 0.75) * mm});
            skLineSegment(sketch, "E47", {"start": v(1.94, 0.75) * mm, "end": v(1.94, 0) * mm});
            skLineSegment(sketch, "E48", {"start": v(1.94, 0) * mm, "end": v(3.24, 0) * mm});
            skSolve(sketch);
        }
        {
            var Q0;
            Q0=makeQuery(id+"F62.imprint","IMPRINT",FACE,{"disambiguationData":[TD([[makeQuery(id+"F62.imprint","IMPRINT",EDGE,{"derivedFrom":sQuery(id+"F62.wireOp",EDGE,"E43")}),-1.0]])]});
            var Q1;
            Q1=makeQuery(id+"F62.imprint","IMPRINT",FACE,{"disambiguationData":[TD([[makeQuery(id+"F62.imprint","IMPRINT",EDGE,{"derivedFrom":sQuery(id+"F62.wireOp",EDGE,"E44")}),-1.0]])]});
            var Q2;
            Q2=makeQuery(id+"F44.opExtrude","CAP_EDGE",EDGE,{"disambiguationData":[OSD([sQuery(id+"F43.wireOp",EDGE,"E30")])],"isStart":false});
            revolve(context, id + "F63", {"operationType" : NewBodyOperationType.REMOVE, "entities" : qUnion([Q0, Q1]), "axis" : qUnion([Q2]), "revolveType" : RevolveType.FULL, "oppositeDirection" : true});
        }
        {
            var Q0;
            Q0=makeQuery(id+"F10.opPattern","COPY",FACE,{"derivedFrom":makeQuery(id+"F9.opPattern","COPY",FACE,{"derivedFrom":makeQuery(id+"F3.opExtrude","CAP_FACE",FACE,{"disambiguationData":[OSD([sQuery(id+"F2.wireOp",EDGE,"E2")])],"isStart":true}),"instanceName":"1"}),"instanceName":"1"});
            var sketch = newSketch(context, id + "F64", { "sketchPlane" : qUnion([Q0])});
            skCircle(sketch, "E49", {"center": v(-29.52, -72.17) * mm, "radius": 1.45 * mm});
            skSolve(sketch);
        }
        {
            var Q0;
            Q0=makeQuery(id+"F64.imprint","IMPRINT",FACE,{"disambiguationData":[TD([[makeQuery(id+"F64.imprint","IMPRINT",EDGE,{"derivedFrom":sQuery(id+"F64.wireOp",EDGE,"E49")}),1.0]])]});
            extrude(context, id + "F65", {"entities" : qUnion([Q0]), "operationType" : NewBodyOperationType.ADD, "depth" : 16 * mm, "offsetDistance" : 25 * mm});
        }
        {
            var Q0;
            Q0=makeQuery(id+"F65.opExtrude","CAP_EDGE",EDGE,{"disambiguationData":[OSD([sQuery(id+"F64.wireOp",EDGE,"E49")])],"isStart":false});
            fillet(context, id + "F66", {"entities" : qUnion([Q0]), "radius" : 0.5 * mm, "tangentPropagation" : true, "allowEdgeOverflow" : false});
        }
    });
